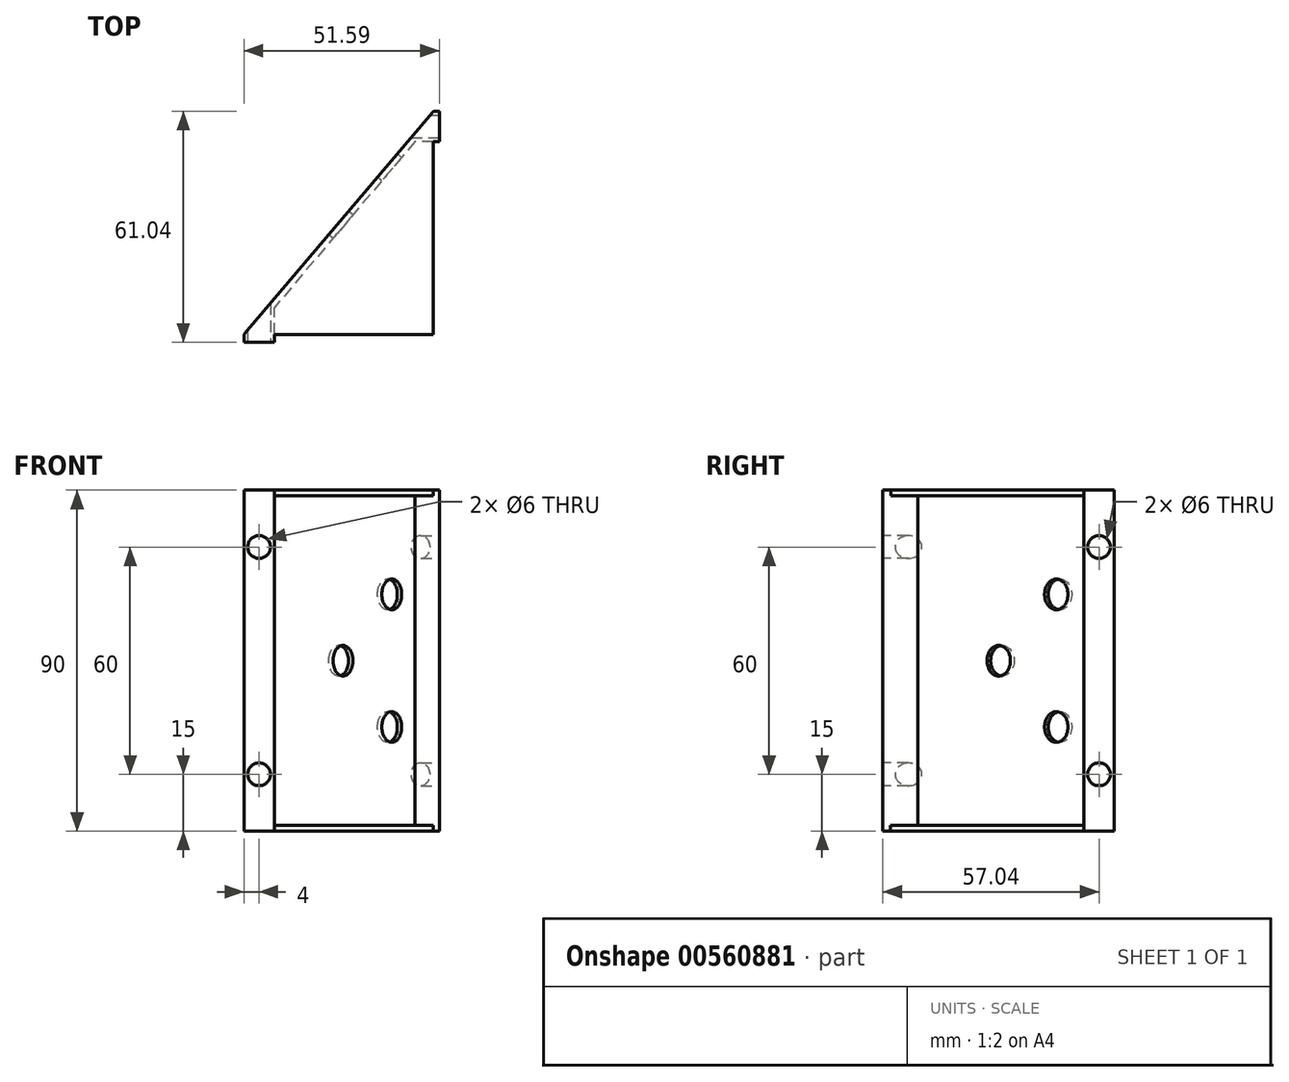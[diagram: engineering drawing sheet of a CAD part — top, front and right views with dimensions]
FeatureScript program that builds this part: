
annotation { "Feature Type Name" : "Feature", "Feature Type Description" : "" }
export const myFeature = defineFeature(function(context is Context, id is Id, definition is map)
    precondition{}
    {
        {
            var Q0;
            Q0=qCreatedBy(makeId("Top.planeOp"),FACE);
            var sketch = newSketch(context, id + "F0", { "sketchPlane" : qUnion([Q0])});
            skLineSegment(sketch, "E0.bottom", {"start": v(0, 0) * mm, "end": v(30, 0) * mm, "construction": true});
            skLineSegment(sketch, "E0.top", {"start": v(0, 30) * mm, "end": v(11, 30) * mm, "construction": true});
            skLineSegment(sketch, "E0.left", {"start": v(0, 0) * mm, "end": v(0, 30) * mm, "construction": true});
            skLineSegment(sketch, "E0.right", {"start": v(30, 0) * mm, "end": v(30, 30) * mm, "construction": true});
            skLineSegment(sketch, "E1.bottom", {"start": v(61, 70) * mm, "end": v(91, 70) * mm, "construction": true});
            skLineSegment(sketch, "E1.top", {"start": v(61, 100) * mm, "end": v(91, 100) * mm, "construction": true});
            skLineSegment(sketch, "E1.left", {"start": v(61, 70) * mm, "end": v(61, 81) * mm, "construction": true});
            skLineSegment(sketch, "E1.right", {"start": v(91, 70) * mm, "end": v(91, 100) * mm, "construction": true});
            skLineSegment(sketch, "E2", {"start": v(91, 100) * mm, "end": v(61, 100) * mm, "construction": true});
            skLineSegment(sketch, "E3", {"start": v(0, 30) * mm, "end": v(0, 0) * mm, "construction": true});
            skLineSegment(sketch, "E4.bottom", {"start": v(61, 89) * mm, "end": v(70, 89) * mm});
            skLineSegment(sketch, "E4.top", {"start": v(61, 81) * mm, "end": v(70, 81) * mm});
            skLineSegment(sketch, "E4.left", {"start": v(61, 89) * mm, "end": v(61, 87.45) * mm});
            skLineSegment(sketch, "E4.right", {"start": v(70, 89) * mm, "end": v(70, 81) * mm});
            skLineSegment(sketch, "E5.top", {"start": v(11, 21) * mm, "end": v(19, 21) * mm});
            skLineSegment(sketch, "E5.left", {"start": v(11, 30) * mm, "end": v(11, 21) * mm});
            skLineSegment(sketch, "E5.right", {"start": v(19, 30) * mm, "end": v(19, 21) * mm});
            skPoint(sketch, "E6.end.orphan", {"position": v(19, 30) * mm});
            skPoint(sketch, "E6.start.orphan", {"position": v(61, 81) * mm});
            skLineSegment(sketch, "E7", {"start": v(19, 30) * mm, "end": v(19, 33.33) * mm});
            skLineSegment(sketch, "E8", {"start": v(61, 81) * mm, "end": v(56.19, 81) * mm});
            skLineSegment(sketch, "E9.trimOffspring", {"start": v(61, 84.36) * mm, "end": v(61, 100) * mm, "construction": true});
            skLineSegment(sketch, "E10.trimOffspring", {"start": v(19, 30) * mm, "end": v(30, 30) * mm, "construction": true});
            skLineSegment(sketch, "E11", {"start": v(61, 89) * mm, "end": v(11, 30) * mm});
            skLineSegment(sketch, "E12", {"start": v(19, 33.33) * mm, "end": v(19, 37.12) * mm});
            skLineSegment(sketch, "E13", {"start": v(56.19, 81) * mm, "end": v(19, 37.12) * mm});
            skPoint(sketch, "E14.orphan", {"position": v(12.97, 30) * mm});
            skLineSegment(sketch, "E15.trimOffspring", {"start": v(13.71, 30) * mm, "end": v(16.26, 30) * mm, "construction": true});
            skLineSegment(sketch, "E16.trimOffspring", {"start": v(61, 87.45) * mm, "end": v(61, 100) * mm, "construction": true});
            skSolve(sketch);
        }
        {
            var Q0;
            Q0=qSketchRegion(id+"F0",true);
            extrude(context, id + "F1", {"entities" : qUnion([Q0]), "depth" : 90 * mm, "offsetDistance" : 25 * mm});
        }
        {
            var Q0;
            Q0=makeQuery(id+"F1.opExtrude","SWEPT_FACE",FACE,{"disambiguationData":[OSD([sQuery(id+"F0.wireOp",EDGE,"E11")])]});
            var sketch = newSketch(context, id + "F2", { "sketchPlane" : qUnion([Q0])});
            skLineSegment(sketch, "E17", {"start": v(-68.67, 90) * mm, "end": v(-68.67, -32.24) * mm, "construction": true});
            skLineSegment(sketch, "E18", {"start": v(-30, 45) * mm, "end": v(-110.72, 45) * mm, "construction": true});
            skCircle(sketch, "E19", {"center": v(-88.58, 27.5) * mm, "radius": 4.05 * mm});
            skCircle(sketch, "E20", {"center": v(-88.58, 62.5) * mm, "radius": 4.05 * mm});
            skCircle(sketch, "E21", {"center": v(-68.67, 45) * mm, "radius": 4.05 * mm});
            skSolve(sketch);
        }
        {
            var Q0;
            Q0=qSketchRegion(id+"F2",true);
            extrude(context, id + "F3", {"entities" : qUnion([Q0]), "operationType" : NewBodyOperationType.REMOVE, "oppositeDirection" : true, "depth" : 25 * mm, "offsetDistance" : 25 * mm});
        }
        {
            var Q0;
            Q0=makeQuery(id+"F1.opExtrude","SWEPT_FACE",FACE,{"disambiguationData":[OSD([sQuery(id+"F0.wireOp",EDGE,"E5.top")])]});
            var sketch = newSketch(context, id + "F4", { "sketchPlane" : qUnion([Q0])});
            skLineSegment(sketch, "E22", {"start": v(15, 90) * mm, "end": v(15, 0) * mm});
            skCircle(sketch, "E23", {"center": v(15, 75) * mm, "radius": 1.75 * mm});
            skCircle(sketch, "E24", {"center": v(15, 15) * mm, "radius": 1.75 * mm});
            skSolve(sketch);
        }
        {
            var Q0;
            Q0=qSketchRegion(id+"F4",true);
            extrude(context, id + "F5", {"entities" : qUnion([Q0]), "operationType" : NewBodyOperationType.REMOVE, "oppositeDirection" : true, "depth" : 25 * mm, "offsetDistance" : 25 * mm});
        }
        {
            var Q0;
            Q0=makeQuery(id+"F1.opExtrude","SWEPT_FACE",FACE,{"disambiguationData":[OSD([sQuery(id+"F0.wireOp",EDGE,"E4.right")])]});
            var sketch = newSketch(context, id + "F6", { "sketchPlane" : qUnion([Q0])});
            skCircle(sketch, "E25", {"center": v(85, 75) * mm, "radius": 1.75 * mm});
            skPoint(sketch, "E25.centerSnap0", {"position": v(85, 90) * mm});
            skCircle(sketch, "E26", {"center": v(85, 15) * mm, "radius": 1.75 * mm});
            skSolve(sketch);
        }
        {
            var Q0;
            Q0=qSketchRegion(id+"F6",true);
            extrude(context, id + "F7", {"entities" : qUnion([Q0]), "operationType" : NewBodyOperationType.REMOVE, "oppositeDirection" : true, "depth" : 25 * mm, "offsetDistance" : 25 * mm});
        }
        {
            var Q0;
            Q0=makeQuery(id+"F1.opExtrude","SWEPT_FACE",FACE,{"disambiguationData":[OSD([sQuery(id+"F0.wireOp",EDGE,"E4.right")])]});
            cPlane(context, id + "F8", {"entities" : qUnion([Q0]), "cplaneType" : CPlaneType.OFFSET, "offset" : 5 * mm, "oppositeDirection" : true, "width" : 150 * mm, "height" : 150 * mm});
        }
        {
            var Q0;
            Q0=qCreatedBy(id+"F8.planeOp",FACE);
            var sketch = newSketch(context, id + "F9", { "sketchPlane" : qUnion([Q0])});
            skCircle(sketch, "E27", {"center": v(85, 75) * mm, "radius": 3 * mm});
            skCircle(sketch, "E28", {"center": v(85, 15) * mm, "radius": 3 * mm});
            skSolve(sketch);
        }
        {
            var Q0;
            Q0=qSketchRegion(id+"F9",true);
            extrude(context, id + "F10", {"entities" : qUnion([Q0]), "operationType" : NewBodyOperationType.REMOVE, "oppositeDirection" : true, "depth" : 25 * mm, "offsetDistance" : 25 * mm});
        }
        {
            var Q0;
            Q0=makeQuery(id+"F1.opExtrude","SWEPT_FACE",FACE,{"disambiguationData":[OSD([sQuery(id+"F0.wireOp",EDGE,"E5.top")])]});
            cPlane(context, id + "F11", {"entities" : qUnion([Q0]), "cplaneType" : CPlaneType.OFFSET, "offset" : 5 * mm, "oppositeDirection" : true, "width" : 150 * mm, "height" : 150 * mm});
        }
        {
            var Q0;
            Q0=qCreatedBy(id+"F11.planeOp",FACE);
            var sketch = newSketch(context, id + "F12", { "sketchPlane" : qUnion([Q0])});
            skCircle(sketch, "E29", {"center": v(15, 75) * mm, "radius": 3 * mm});
            skCircle(sketch, "E30", {"center": v(15, 15) * mm, "radius": 3 * mm});
            skSolve(sketch);
        }
        {
            var Q0;
            Q0=qSketchRegion(id+"F12",true);
            extrude(context, id + "F13", {"entities" : qUnion([Q0]), "operationType" : NewBodyOperationType.REMOVE, "oppositeDirection" : true, "depth" : 25 * mm, "offsetDistance" : 25 * mm});
        }
        {
            var Q0;
            Q0=makeQuery(id+"F1.opExtrude","SWEPT_EDGE",EDGE,{"disambiguationData":[OSD([sQuery(id+"F0.wireOp",EDGE,"E4.top"),sQuery(id+"F0.wireOp",EDGE,"E4.right")])]});
            var Q1;
            Q1=makeQuery(id+"F1.opExtrude","SWEPT_EDGE",EDGE,{"disambiguationData":[OSD([sQuery(id+"F0.wireOp",EDGE,"E4.bottom"),sQuery(id+"F0.wireOp",EDGE,"E4.right")])]});
            var Q2;
            Q2=makeQuery(id+"F1.opExtrude","SWEPT_EDGE",EDGE,{"disambiguationData":[OSD([sQuery(id+"F0.wireOp",EDGE,"E5.top"),sQuery(id+"F0.wireOp",EDGE,"E5.right")])]});
            var Q3;
            Q3=makeQuery(id+"F1.opExtrude","SWEPT_EDGE",EDGE,{"disambiguationData":[OSD([sQuery(id+"F0.wireOp",EDGE,"E5.top"),sQuery(id+"F0.wireOp",EDGE,"E5.left")])]});
            chamfer(context, id + "F14", {"entities" : qUnion([Q0, Q1, Q2, Q3]), "width" : 2 * mm, "tangentPropagation" : true});
        }
        {
            var Q0;
            Q0=makeQuery(id+"F1.opExtrude","SWEPT_EDGE",EDGE,{"disambiguationData":[OSD([sQuery(id+"F0.wireOp",EDGE,"E4.bottom"),sQuery(id+"F0.wireOp",EDGE,"E11")])]});
            var Q1;
            Q1=makeQuery(id+"F1.opExtrude","SWEPT_EDGE",EDGE,{"disambiguationData":[OSD([sQuery(id+"F0.wireOp",EDGE,"E5.left"),sQuery(id+"F0.wireOp",EDGE,"E11")])]});
            fillet(context, id + "F15", {"entities" : qUnion([Q0, Q1]), "radius" : 1 * mm, "tangentPropagation" : true, "allowEdgeOverflow" : false});
        }
        {
            var Q0;
            Q0=makeQuery(id+"F1.opExtrude","CAP_FACE",FACE,{"disambiguationData":[OSD([sQuery(id+"F0.wireOp",EDGE,"E4.bottom"),sQuery(id+"F0.wireOp",EDGE,"E4.top"),sQuery(id+"F0.wireOp",EDGE,"E4.right"),sQuery(id+"F0.wireOp",EDGE,"E5.top"),sQuery(id+"F0.wireOp",EDGE,"E5.left"),sQuery(id+"F0.wireOp",EDGE,"E5.right"),sQuery(id+"F0.wireOp",EDGE,"E7"),sQuery(id+"F0.wireOp",EDGE,"E8"),sQuery(id+"F0.wireOp",EDGE,"E11"),sQuery(id+"F0.wireOp",EDGE,"E12"),sQuery(id+"F0.wireOp",EDGE,"E13")])],"isStart":false});
            var sketch = newSketch(context, id + "F16", { "sketchPlane" : qUnion([Q0])});
            skLineSegment(sketch, "E31", {"start": v(19, 30.06) * mm, "end": v(61, 30.06) * mm});
            skPoint(sketch, "E32.startSnap0", {"position": v(62.1, 81) * mm});
            skLineSegment(sketch, "E33", {"start": v(61, 81) * mm, "end": v(61, 30.06) * mm});
            skLineSegment(sketch, "E34", {"start": v(61, 81) * mm, "end": v(56.19, 81) * mm});
            skLineSegment(sketch, "E35", {"start": v(56.19, 81) * mm, "end": v(19, 37.12) * mm});
            skLineSegment(sketch, "E36", {"start": v(19, 37.12) * mm, "end": v(19, 30.06) * mm});
            skSolve(sketch);
        }
        {
            var Q0;
            Q0=qSketchRegion(id+"F16",true);
            extrude(context, id + "F17", {"entities" : qUnion([Q0]), "operationType" : NewBodyOperationType.ADD, "oppositeDirection" : true, "depth" : 1.5 * mm, "offsetDistance" : 25 * mm});
        }
        {
            var Q0;
            Q0=makeQuery(id+"F0.imprint","IMPRINT",FACE,{"disambiguationData":[TD([[makeQuery(id+"F0.imprint","IMPRINT",EDGE,{"derivedFrom":sQuery(id+"F0.wireOp",EDGE,"E4.bottom")}),-1.0]])]});
            var sketch = newSketch(context, id + "F18", { "sketchPlane" : qUnion([Q0])});
            skLineSegment(sketch, "E37", {"start": v(61, 81) * mm, "end": v(61, 30) * mm});
            skLineSegment(sketch, "E38", {"start": v(19, 30) * mm, "end": v(61, 30) * mm});
            skLineSegment(sketch, "E39", {"start": v(19, 30) * mm, "end": v(19, 37.12) * mm});
            skLineSegment(sketch, "E40", {"start": v(19, 37.12) * mm, "end": v(56.19, 81) * mm});
            skLineSegment(sketch, "E41", {"start": v(56.19, 81) * mm, "end": v(61, 81) * mm});
            skSolve(sketch);
        }
        {
            var Q0;
            Q0=qSketchRegion(id+"F18",true);
            extrude(context, id + "F19", {"entities" : qUnion([Q0]), "operationType" : NewBodyOperationType.ADD, "depth" : 1.5 * mm, "offsetDistance" : 25 * mm});
        }
        {
            var Q0;
            Q0=makeQuery(id+"F17.boolean.opBoolean","MERGE",FACE,{"derivedFrom":[makeQuery(id+"F1.opExtrude","CAP_FACE",FACE,{"disambiguationData":[OSD([sQuery(id+"F0.wireOp",EDGE,"E4.bottom"),sQuery(id+"F0.wireOp",EDGE,"E4.top"),sQuery(id+"F0.wireOp",EDGE,"E4.right"),sQuery(id+"F0.wireOp",EDGE,"E5.top"),sQuery(id+"F0.wireOp",EDGE,"E5.left"),sQuery(id+"F0.wireOp",EDGE,"E5.right"),sQuery(id+"F0.wireOp",EDGE,"E7"),sQuery(id+"F0.wireOp",EDGE,"E8"),sQuery(id+"F0.wireOp",EDGE,"E11"),sQuery(id+"F0.wireOp",EDGE,"E12"),sQuery(id+"F0.wireOp",EDGE,"E13")])],"isStart":false}),makeQuery(id+"F17.opExtrude","CAP_FACE",FACE,{"disambiguationData":[OSD([sQuery(id+"F16.wireOp",EDGE,"E31"),sQuery(id+"F16.wireOp",EDGE,"E33"),sQuery(id+"F16.wireOp",EDGE,"E34"),sQuery(id+"F16.wireOp",EDGE,"E35"),sQuery(id+"F16.wireOp",EDGE,"E36")])],"isStart":true})]});
            var sketch = newSketch(context, id + "F20", { "sketchPlane" : qUnion([Q0])});
            skLineSegment(sketch, "E42", {"start": v(62.6, 90.23) * mm, "end": v(62.6, 79.75) * mm});
            skLineSegment(sketch, "E43", {"start": v(62.6, 79.75) * mm, "end": v(71.94, 79.75) * mm});
            skLineSegment(sketch, "E44", {"start": v(71.94, 79.75) * mm, "end": v(71.94, 90.23) * mm});
            skLineSegment(sketch, "E45", {"start": v(71.94, 90.23) * mm, "end": v(62.6, 90.23) * mm});
            skLineSegment(sketch, "E46.bottom", {"start": v(9.56, 27.96) * mm, "end": v(21.3, 27.96) * mm});
            skLineSegment(sketch, "E46.top", {"start": v(9.56, 19.88) * mm, "end": v(21.3, 19.88) * mm});
            skLineSegment(sketch, "E46.left", {"start": v(9.56, 27.96) * mm, "end": v(9.56, 19.88) * mm});
            skLineSegment(sketch, "E46.right", {"start": v(21.3, 27.96) * mm, "end": v(21.3, 19.88) * mm});
            skSolve(sketch);
        }
        {
            var Q0;
            Q0 = qSketchRegion(id + "F20", true);
            extrude(context, id + "F21", {"entities" : qUnion([Q0]), "operationType" : NewBodyOperationType.REMOVE, "endBound" : BoundingType.THROUGH_ALL, "oppositeDirection" : true, "depth" : 25 * mm, "offsetDistance" : 25 * mm});
        }
    });
